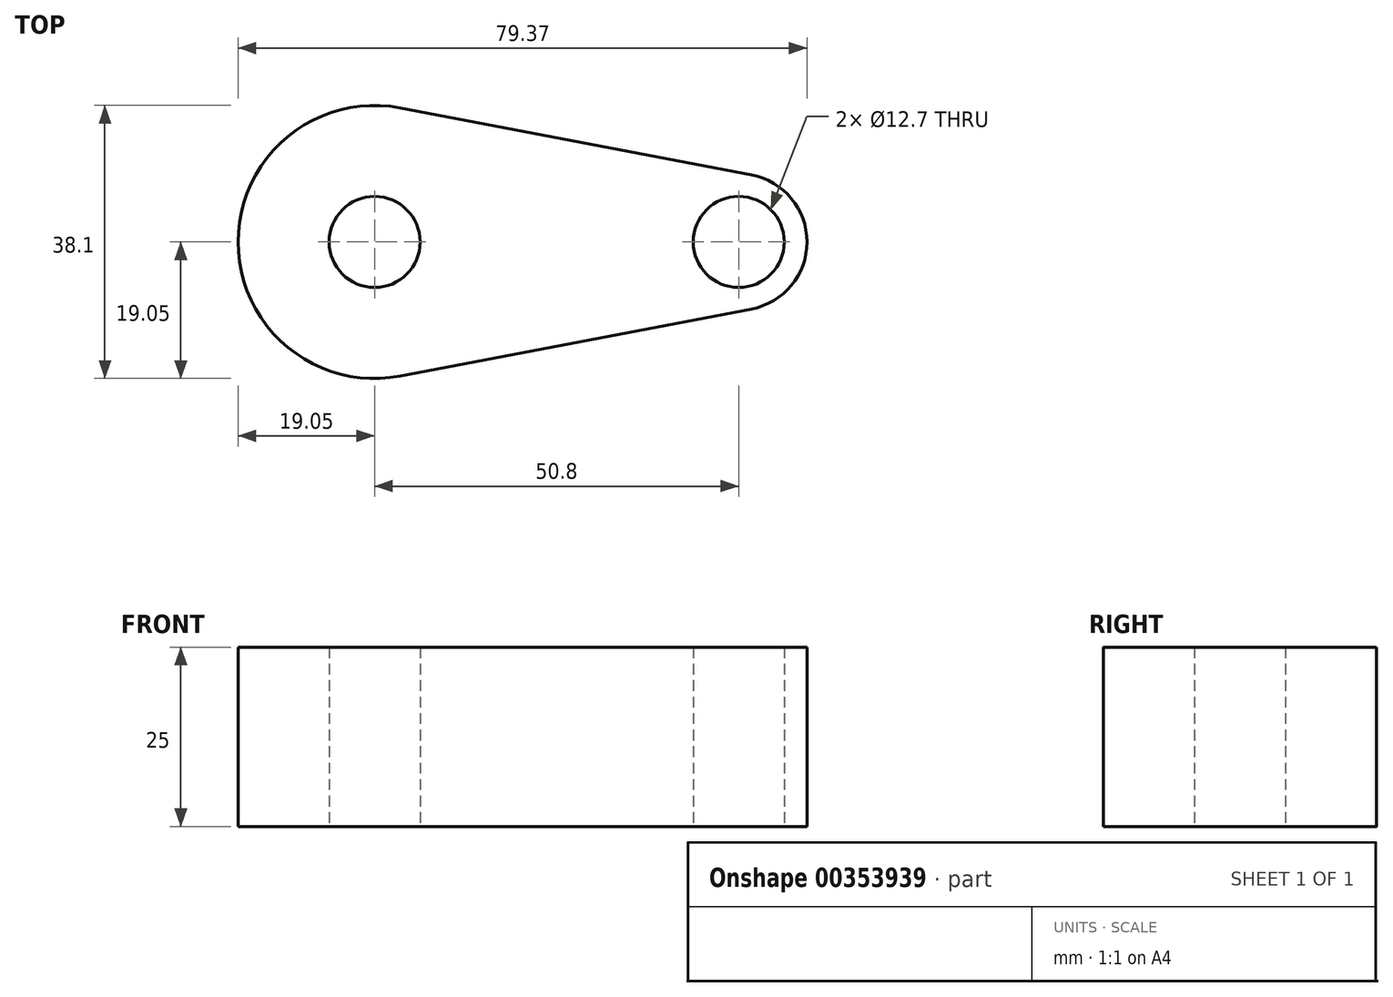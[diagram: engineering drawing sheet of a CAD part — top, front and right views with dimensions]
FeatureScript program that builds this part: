
annotation { "Feature Type Name" : "Feature", "Feature Type Description" : "" }
export const myFeature = defineFeature(function(context is Context, id is Id, definition is map)
    precondition{}
    {
        {
            var Q0;
            Q0=qCreatedBy(makeId("Top.planeOp"),FACE);
            var sketch = newSketch(context, id + "F0", { "sketchPlane" : qUnion([Q0])});
            skLineSegment(sketch, "E0", {"start": v(0, 0) * mm, "end": v(50.8, 0) * mm, "construction": true});
            skCircle(sketch, "E1", {"center": v(0, 0) * mm, "radius": 6.35 * mm});
            skCircle(sketch, "E2", {"center": v(50.8, 0) * mm, "radius": 6.35 * mm});
            skCircle(sketch, "E3", {"center": v(0, 0) * mm, "radius": 19.05 * mm});
            skCircle(sketch, "E4", {"center": v(50.8, 0) * mm, "radius": 9.53 * mm});
            skLineSegment(sketch, "E5", {"start": v(3.57, 18.71) * mm, "end": v(52.59, 9.36) * mm});
            skLineSegment(sketch, "E6", {"start": v(3.57, -18.71) * mm, "end": v(52.59, -9.36) * mm});
            skPoint(sketch, "E7.orphan", {"position": v(0, -19.4) * mm});
            skSolve(sketch);
        }
        {
            var Q0;
            Q0=makeQuery(id+"F0.imprint","IMPRINT",FACE,{"disambiguationData":[TD([[makeQuery(id+"F0.imprint","IMPRINT",EDGE,{"derivedFrom":sQuery(id+"F0.wireOp",EDGE,"E2")}),-1.0]])]});
            var Q1;
            {var subQ0=sQuery(id+"F0.wireOp",EDGE,"E5");Q1=makeQuery(id+"F0.imprint","IMPRINT",FACE,{"disambiguationData":[TD([[makeQuery(id+"F0.imprint","IMPRINT",EDGE,{"derivedFrom":subQ0}),-1.0]])]});}
            var Q2;
            Q2=makeQuery(id+"F0.imprint","IMPRINT",FACE,{"disambiguationData":[TD([[makeQuery(id+"F0.imprint","IMPRINT",EDGE,{"derivedFrom":sQuery(id+"F0.wireOp",EDGE,"E1")}),-1.0]])]});
            extrude(context, id + "F1", {"entities" : qUnion([Q0, Q1, Q2]), "depth" : 25 * mm});
        }
    });
